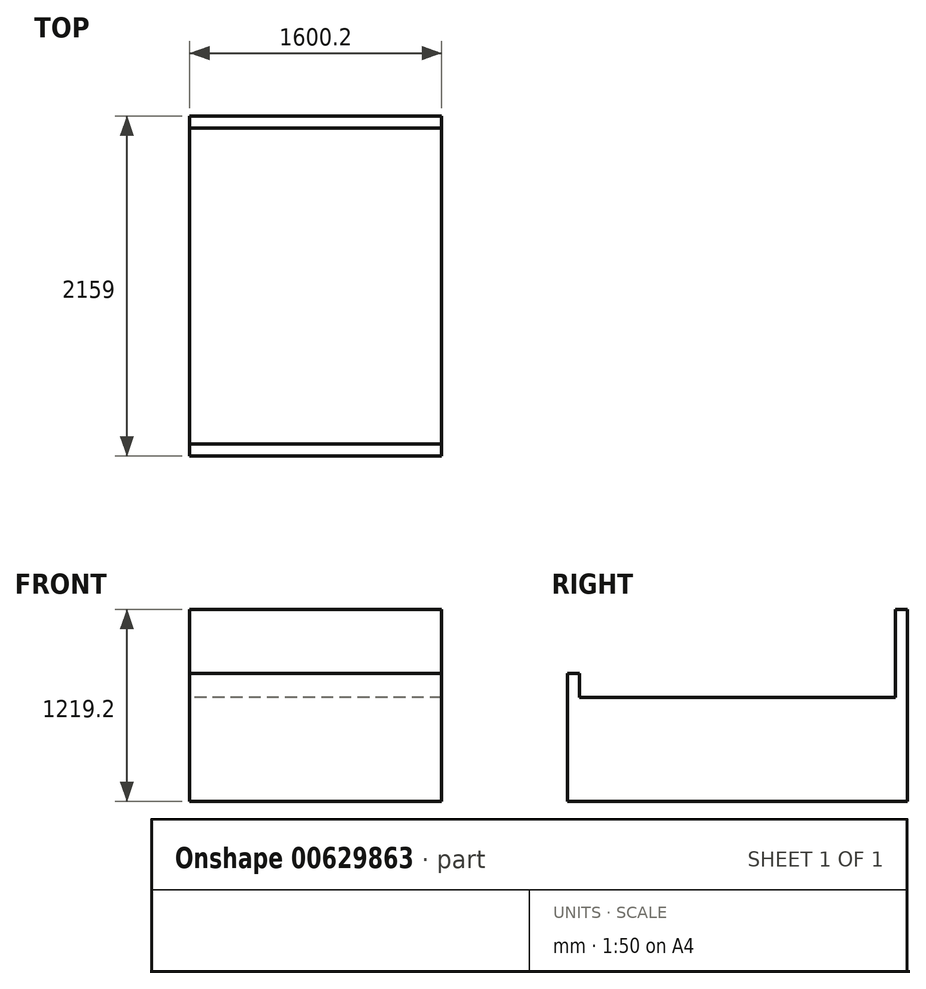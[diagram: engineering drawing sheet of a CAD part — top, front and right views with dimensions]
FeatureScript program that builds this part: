
annotation { "Feature Type Name" : "Feature", "Feature Type Description" : "" }
export const myFeature = defineFeature(function(context is Context, id is Id, definition is map)
    precondition{}
    {
        {
            var Q0;
            Q0=qCreatedBy(makeId("Top.planeOp"),FACE);
            var sketch = newSketch(context, id + "F0", { "sketchPlane" : qUnion([Q0])});
            skLineSegment(sketch, "E0.bottom", {"start": v(0, 0) * mm, "end": v(1600.2, 0) * mm});
            skLineSegment(sketch, "E0.top", {"start": v(0, 2159) * mm, "end": v(1600.2, 2159) * mm});
            skLineSegment(sketch, "E0.left", {"start": v(0, 0) * mm, "end": v(0, 2159) * mm});
            skLineSegment(sketch, "E0.right", {"start": v(1600.2, 0) * mm, "end": v(1600.2, 2159) * mm});
            skLineSegment(sketch, "E1.top", {"start": v(0, 2082.8) * mm, "end": v(1600.2, 2082.8) * mm});
            skLineSegment(sketch, "E1.left", {"start": v(0, 2159) * mm, "end": v(0, 2082.8) * mm});
            skLineSegment(sketch, "E1.right", {"start": v(1600.2, 2159) * mm, "end": v(1600.2, 2082.8) * mm});
            skLineSegment(sketch, "E2.top", {"start": v(0, 76.2) * mm, "end": v(1600.2, 76.2) * mm});
            skLineSegment(sketch, "E2.left", {"start": v(0, 0) * mm, "end": v(0, 76.2) * mm});
            skLineSegment(sketch, "E2.right", {"start": v(1600.2, 0) * mm, "end": v(1600.2, 76.2) * mm});
            skSolve(sketch);
        }
        {
            var Q0;
            Q0=makeQuery(id+"F0.imprint","IMPRINT",FACE,{"disambiguationData":[TD([[makeQuery(id+"F0.imprint","IMPRINT",EDGE,{"derivedFrom":sQuery(id+"F0.wireOp",EDGE,"E0.left")}),-1.0]])]});
            extrude(context, id + "F1", {"entities" : qUnion([Q0]), "depth" : 660.4 * mm, "offsetDistance" : 25.4 * mm});
        }
        {
            var Q0;
            Q0=makeQuery(id+"F0.imprint","IMPRINT",FACE,{"disambiguationData":[TD([[makeQuery(id+"F0.imprint","IMPRINT",EDGE,{"derivedFrom":sQuery(id+"F0.wireOp",EDGE,"E0.top")}),-1.0]])]});
            extrude(context, id + "F2", {"entities" : qUnion([Q0]), "operationType" : NewBodyOperationType.ADD, "depth" : 1219.2 * mm, "offsetDistance" : 25.4 * mm});
        }
        {
            var Q0;
            Q0=makeQuery(id+"F0.imprint","IMPRINT",FACE,{"disambiguationData":[TD([[makeQuery(id+"F0.imprint","IMPRINT",EDGE,{"derivedFrom":sQuery(id+"F0.wireOp",EDGE,"E0.bottom")}),1.0]])]});
            extrude(context, id + "F3", {"entities" : qUnion([Q0]), "operationType" : NewBodyOperationType.ADD, "depth" : 812.8 * mm, "offsetDistance" : 25.4 * mm});
        }
    });
